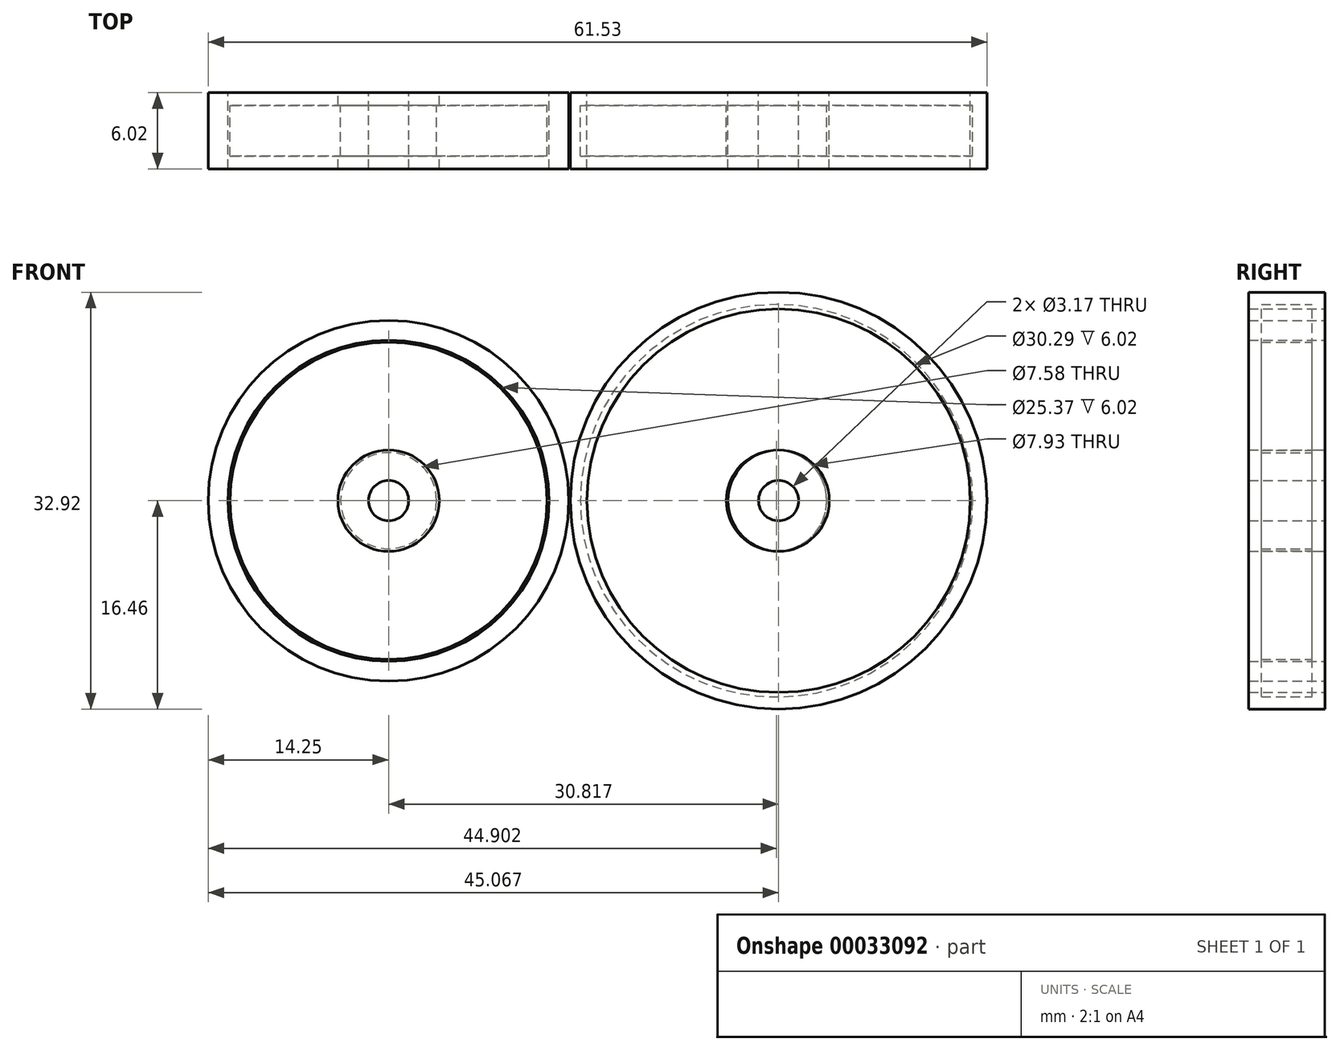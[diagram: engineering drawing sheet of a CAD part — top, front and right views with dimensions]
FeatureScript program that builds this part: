
annotation { "Feature Type Name" : "Feature", "Feature Type Description" : "" }
export const myFeature = defineFeature(function(context is Context, id is Id, definition is map)
    precondition{}
    {
        {
            var Q0;
            Q0=qCreatedBy(makeId("Front.planeOp"),FACE);
            var sketch = newSketch(context, id + "F0", { "sketchPlane" : qUnion([Q0])});
            skCircle(sketch, "E0", {"center": v(0, 0) * mm, "radius": 14.25 * mm});
            skCircle(sketch, "E1", {"center": v(30.82, 0) * mm, "radius": 16.46 * mm});
            skCircle(sketch, "E2", {"center": v(0, 0) * mm, "radius": 12.69 * mm});
            skCircle(sketch, "E3", {"center": v(0, 0) * mm, "radius": 4 * mm});
            skCircle(sketch, "E4", {"center": v(30.82, 0) * mm, "radius": 4 * mm});
            skCircle(sketch, "E5", {"center": v(30.82, 0) * mm, "radius": 15.14 * mm});
            skCircle(sketch, "E6", {"center": v(0, 0) * mm, "radius": 1.59 * mm});
            skCircle(sketch, "E7", {"center": v(30.82, 0) * mm, "radius": 1.59 * mm});
            skSolve(sketch);
        }
        {
            var Q0;
            Q0=makeQuery(id+"F0.imprint","IMPRINT",FACE,{"disambiguationData":[TD([[makeQuery(id+"F0.imprint","IMPRINT",EDGE,{"derivedFrom":sQuery(id+"F0.wireOp",EDGE,"E3")}),1.0]])]});
            var Q1;
            Q1=makeQuery(id+"F0.imprint","IMPRINT",FACE,{"disambiguationData":[TD([[makeQuery(id+"F0.imprint","IMPRINT",EDGE,{"derivedFrom":sQuery(id+"F0.wireOp",EDGE,"E4")}),1.0]])]});
            extrude(context, id + "F1", {"entities" : qUnion([Q0, Q1]), "endBound" : BoundingType.SYMMETRIC, "depth" : 6.02 * mm});
        }
        {
            var Q0;
            Q0 = qSketchRegion(id + "F0", true);
            extrude(context, id + "F2", {"entities" : qUnion([Q0]), "endBound" : BoundingType.SYMMETRIC, "depth" : 6.02 * mm});
        }
        {
            var Q0;
            Q0=qCreatedBy(makeId("Front.planeOp"),FACE);
            var sketch = newSketch(context, id + "F3", { "sketchPlane" : qUnion([Q0])});
            skCircle(sketch, "E8", {"center": v(0, 0) * mm, "radius": 12.53 * mm});
            skCircle(sketch, "E9", {"center": v(0, 0) * mm, "radius": 3.79 * mm});
            skCircle(sketch, "E10", {"center": v(30.65, 0) * mm, "radius": 15.5 * mm});
            skCircle(sketch, "E11", {"center": v(30.65, 0) * mm, "radius": 3.97 * mm});
            skSolve(sketch);
        }
        {
            var Q0;
            Q0=makeQuery(id+"F3.imprint","IMPRINT",FACE,{"disambiguationData":[TD([[makeQuery(id+"F3.imprint","IMPRINT",EDGE,{"derivedFrom":sQuery(id+"F3.wireOp",EDGE,"E8")}),1.0]])]});
            extrude(context, id + "F4", {"entities" : qUnion([Q0]), "operationType" : NewBodyOperationType.ADD, "endBound" : BoundingType.SYMMETRIC, "depth" : 4 * mm});
        }
        {
            var Q0;
            Q0 = qSketchRegion(id + "F3", true);
            extrude(context, id + "F5", {"entities" : qUnion([Q0]), "endBound" : BoundingType.SYMMETRIC, "depth" : 4 * mm});
        }
    });
